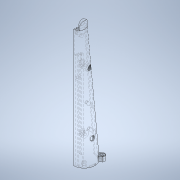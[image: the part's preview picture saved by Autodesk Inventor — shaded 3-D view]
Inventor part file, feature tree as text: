
AUTODESK INVENTOR PART (.ipt)
format: ipt  version: 2021 (Build 250183000, 183)  size: 860,672 bytes
history: native  units: mm
features: sketch x35, extrude x30, plane x15, fillet x4, hole x3, loft x2, revolve x2, other x1, thread x1
ambient origin geometry x8: Origin, YZ Plane, XZ Plane, XY Plane, X Axis, Y Axis, Z Axis, Center Point
bodies: Body1 (feature_tree)
feature tree (93):
  other  "Sólido1"
  plane  "Plano de trabajo1"
  plane  "Plano de trabajo2"
  plane  "Plano de trabajo4"
  plane  "Plano de trabajo5"
  plane  "Plano de trabajo6"
  sketch  "Boceto1"  dims[d1=250.0mm d2=0.0mm d3=-80.0mm d4=-110.0mm]
  sketch  "Boceto2"  dims[d5=-140.0mm d7=-0.0mm d8=2.0mm]
  sketch  "Boceto3"  dims[d9=140.0mm d10=250.0mm]
  sketch  "Boceto4"  dims[d11=24.0mm d22=0.0mm d23=90.0deg d24=0.0mm d25=90.0deg]
  sketch  "Boceto6"  dims[d44=45.0mm d49=29.11157mm]
  sketch  "Boceto7"  dims[d50=29.11157mm d53=29.11157mm]
  loft  "Solevación1"
  fillet  "Empalme2"  [1 undecoded]
  extrude  "Extrusión1"  TaperAngle=0.0deg  [1 undecoded]
  fillet  "Empalme5"  Radius=2.0mm
  plane  "Plano de trabajo7"
  extrude  "Extrusión2"  Depth=250.0mm
  plane  "Plano de trabajo8"
  plane  "Plano de trabajo9"
  loft  "Solevación9"
  plane  "Plano de trabajo10"
  extrude  "Extrusión3"  Depth=29.11157mm
  plane  "Plano de trabajo11"
  revolve  "Revolución1"  [1 undecoded]
  revolve  "Revolución2"  [1 undecoded]
  extrude  "Extrusión4"  Depth=32.5mm
  plane  "Plano de trabajo12"
  extrude  "Extrusión5"  Depth=44.747934mm
  plane  "Plano de trabajo13"
  plane  "Plano de trabajo14"
  extrude  "Extrusión6"  Depth=42.747934mm
  extrude  "Extrusión7"  Depth=42.747934mm
  extrude  "Extrusión8"  Depth=13.0mm
  extrude  "Extrusión11"  Depth=7.75mm
  extrude  "Extrusión9"  Depth=7.75mm
  extrude  "Extrusión10"  Depth=16.0mm
  extrude  "Extrusión12"  Depth=12.0mm
  sketch  "Boceto30"  dims[d160=-19.75mm d161=0.0mm d163=0.0mm d164=2.0mm]
  extrude  "Extrusión13"  Depth=7.75mm
  extrude  "Extrusión14"  Depth=7.75mm
  extrude  "Extrusión15"  TaperAngle=0.0deg  [1 undecoded]
  hole  "Agujero1"  [1 undecoded]
  thread  "Rosca1"  [1 undecoded]
  extrude  "Extrusión16"  Depth=2.0mm
  plane  "Plano de trabajo16"
  extrude  "Extrusión17"  TaperAngle=0.0deg  [1 undecoded]
  extrude  "Extrusión18"  TaperAngle=0.0deg  [1 undecoded]
  fillet  "Empalme6"  [1 undecoded]
  fillet  "Empalme7"  Radius=2.0mm
  plane  "Plano de trabajo17"
  sketch  "Boceto46"  dims[d185=2.0mm d187=1.0mm]
  hole  "Agujero2"  [1 undecoded]
  hole  "Agujero3"  [1 undecoded]
  extrude  "Extrusión21"  [1 undecoded]
  sketch  "Boceto44"  dims[d181=0.75mm d182=0.25mm]
  extrude  "Extrusión23"  Depth=0.75mm
  sketch  "Boceto47"  dims[d189=3.0mm d190=2.0mm]
  extrude  "Extrusión22"  Depth=1.0mm
  sketch  "Boceto45"  dims[d183=1.0mm d184=0.25mm]
  extrude  "Extrusión32"  Depth=17.453293mm
  extrude  "Extrusión29"  Depth=0.75mm
  extrude  "Extrusión30"  Depth=0.25mm
  extrude  "Extrusión31"  Depth=0.25mm
  extrude  "Extrusión26"  Depth=1.0mm
  extrude  "Extrusión27"  Depth=3.0mm
  extrude  "Extrusión28"  Depth=10.0mm
  sketch  "Boceto49"  dims[d191=2.0mm d192=0.25mm d193=0.25mm d194=90.0deg d196=4.381635mm d197=0.0mm d198=-48.25mm d199=12.0mm d200=20.0mm d201=9.0mm d202=9.0mm d203=2.0mm d204=201.75mm d205=0.0mm d206=0.5mm d207=0.25mm d208=-7.5mm d209=100.0mm d210=0.0mm d211=35.0mm d212=0.0mm d213=210.0mm d214=0.0mm d215=2.0mm d216=1.059606mm d217=6.5mm d218=1.059606mm d219=5.0mm d220=2.0mm d221=0.0mm d222=2.0mm d223=6.5mm d224=1.059606mm d225=5.0mm d226=4.5mm d227=2.0mm d228=0.0mm d229=6.0mm d230=10.0mm d231=3.0mm d232=11.0mm d233=10.5mm d235=30.0deg d236=4.75mm d237=0.0mm d238=-17.0mm d239=100.0mm d240=0.0mm d241=6.5mm d242=2.0mm d243=4.0mm d244=15.0mm d245=2.0mm d247=16.0mm d248=2.0mm d249=0.0mm d250=4.5mm d251=0.75mm d252=2.5mm d253=1.0mm d254=11.0mm d255=17.453293mm d256=2.939597mm d257=0.75mm d258=0.75mm d259=0.25mm d260=1.0mm d261=0.25mm d262=2.0mm d263=1.0mm d264=3.0mm d265=2.0mm d266=2.0mm d267=0.25mm d268=0.25mm d269=40.0mm d270=1.0mm d271=1.0mm d272=7.75mm d273=0.5mm d274=8.5mm d275=90.0deg d276=0.0mm d277=17.75mm d280=22.5mm d281=2.0mm d282=0.0mm d283=0.0mm d292=2.0mm d293=0.0mm d296=3.5mm d297=0.0mm d299=4.0mm d300=3.708mm d301=3.023mm d302=2.0mm d303=14.3117mm d304=16.0mm d305=0.0mm d306=16.0mm d307=0.0mm d314=6.0mm d315=19.2mm d316=6.0mm d317=19.2mm d318=13.0mm d320=6.0mm d321=19.2mm d322=13.0mm d323=6.0mm d324=19.2mm d325=13.0mm d326=7.0mm d332=10.0mm d333=0.0mm d335=-41.0mm d336=4.0mm d337=1.0mm d338=9.0mm d339=4.0mm d340=1.0mm d341=9.0mm d342=4.0mm d343=5.2mm d344=4.0mm d345=0.0mm d346=15.0mm d347=5.0mm d349=5.0mm d351=0.0mm d352=45.0mm d354=10.0mm d355=10.0mm d356=0.0mm d357=15.0mm d358=0.0mm d359=2.0mm d363=50.4375mm d376=14.059606mm d377=2.0mm d378=0.0mm d379=2.0mm d380=11.25mm d381=90.0mm d382=290.0mm d383=14.059606mm d384=100.875mm d390=30.940394mm d391=2.0mm d392=100.875mm d393=14.790546mm d394=2.0mm d395=3.0mm d396=6.0mm d397=4.0mm d398=4.0mm d399=4.0mm d400=8.128453mm d401=12.0mm d402=5.5mm d403=2.5mm d404=2.0mm d405=2.0mm d406=1.0mm d407=2.0mm d408=2.0mm d409=0.0mm d411=50.4375mm d412=6.0mm d418=13.059606mm d419=6.5mm d420=6.5mm d421=50.4375mm d422=126.09375mm d423=0.0mm d424=15.0mm d425=5.0mm d426=5.0mm d427=0.0mm d428=45.0mm d429=10.0mm d430=2.0mm d431=4.0mm d432=6.0mm d433=8.0mm d434=2.0mm d435=90.0deg d436=20.0mm d437=0.0mm d438=4.0mm d439=6.0mm d440=8.0mm d441=2.0mm d442=90.0deg d443=20.0mm d444=0.0mm d446=10.0mm d447=3.0mm d448=11.5mm d450=9.0mm d451=9.0mm d452=90.0mm d453=750.0mm d454=22.5mm d455=43.0mm d456=44.0mm d457=14.059606mm d458=11.25mm d459=2.0mm d460=0.0mm d461=22.5mm d462=43.0mm d463=7.059606mm d464=3.0mm d465=6.0mm d466=3.0mm d467=6.0mm d468=180.0mm d469=0.0mm d470=180.0mm d471=0.0mm d472=4.5mm d473=10.0mm d474=0.0mm d475=7.0mm d476=0.0mm d477=0.0mm d478=0.0mm d479=6.0mm d480=0.0mm d481=14.059606mm d482=250.0mm d483=2.0mm d484=0.0mm d485=4.2mm d486=4.2mm d487=4.2mm d488=7.0mm d489=0.0mm d490=2.0mm d491=0.0mm d492=4.0mm d493=4.0mm d494=0.0mm d495=0.0mm d496=0.0mm d497=0.0mm]
  extrude  "Extrusión24"  Depth=10.0mm
  extrude  "Extrusión25"  TaperAngle=90.0deg  [1 undecoded]
  sketch  "Boceto9"  dims[d59=29.11157mm d61=29.11157mm]
  sketch  "Boceto10"  dims[d65=22.5mm d66=32.5mm]
  sketch  "Boceto15"  dims[d67=22.5mm d90=44.747934mm]
  sketch  "Boceto16"  dims[d91=42.747934mm d93=42.747934mm]
  sketch  "Boceto17"  dims[d96=0.0mm d97=90.0deg d98=0.0mm d99=90.0deg d100=0.0mm d101=90.0deg d102=0.0mm d103=90.0deg d112=42.747934mm]
  sketch  "Boceto18"  dims[d115=5.0mm d120=13.0mm]
  sketch  "Boceto19"  dims[d121=6.5mm d124=7.75mm]
  sketch  "Boceto20"  dims[d125=7.75mm d126=7.75mm]
  sketch  "Boceto21"  dims[d127=7.75mm d130=16.0mm]
  sketch  "Boceto22"  dims[d131=0.0mm d132=12.0mm]
  sketch  "Boceto24"  dims[d133=12.0mm d134=7.75mm]
  sketch  "Boceto25"  dims[d135=6.5mm d136=7.75mm]
  sketch  "Boceto26"  dims[d137=15.0mm d138=0.0mm]
  sketch  "Boceto27"  dims[d146=-8.5mm d147=30.0mm d148=2.0mm]
  sketch  "Boceto28"  dims[d149=25.12mm d150=2.0mm]
  sketch  "Boceto29"  dims[d151=10.357mm d156=0.0mm d157=90.0deg d158=0.0mm d159=90.0deg]
  sketch  "Boceto31"  dims[d165=15.0mm d166=4.0mm]
  sketch  "Boceto36"  dims[d167=30.0mm d168=12.0mm]
  sketch  "Boceto37"  dims[d169=0.0mm d170=-7.25mm]
  sketch  "Boceto38"  dims[d171=4.5mm d172=0.75mm]
  sketch  "Boceto39"  dims[d173=2.5mm d174=1.0mm]
  sketch  "Boceto40"  dims[d176=11.0mm d177=17.453293mm]
  sketch  "Boceto41"  dims[d179=2.939597mm d180=0.75mm]
note: 14 required parameter values undecoded (feature->parameter linkage not recoverable at this tier; creation-order binding heuristic only, values carry confidence <= 0.55)